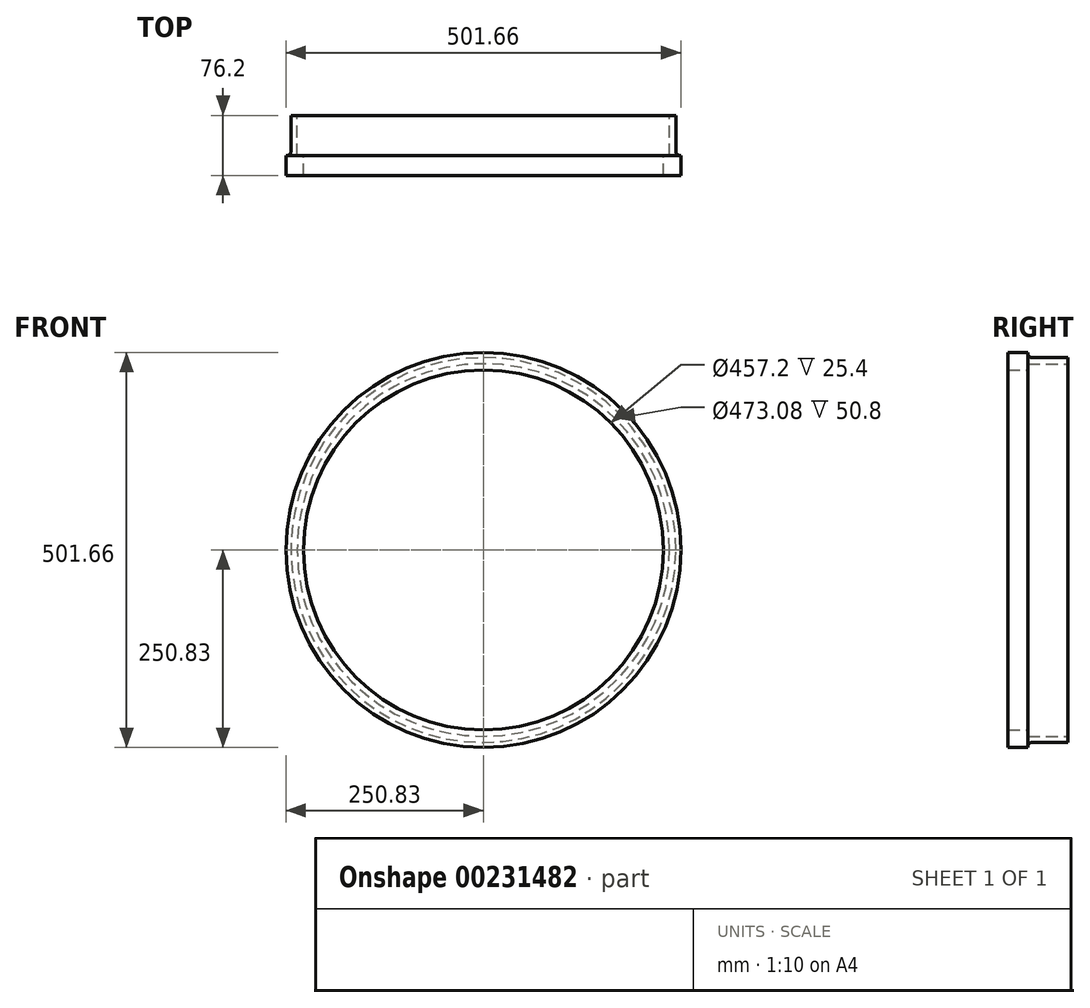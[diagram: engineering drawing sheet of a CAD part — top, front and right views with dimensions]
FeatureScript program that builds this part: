
annotation { "Feature Type Name" : "Feature", "Feature Type Description" : "" }
export const myFeature = defineFeature(function(context is Context, id is Id, definition is map)
    precondition{}
    {
        {
            var Q0;
            Q0=qCreatedBy(makeId("Front.planeOp"),FACE);
            var sketch = newSketch(context, id + "F0", { "sketchPlane" : qUnion([Q0])});
            skCircle(sketch, "E0", {"center": v(0, 0) * mm, "radius": 250.83 * mm});
            skCircle(sketch, "E1", {"center": v(0, 0) * mm, "radius": 228.6 * mm});
            skSolve(sketch);
        }
        {
            var Q0;
            Q0 = qSketchRegion(id + "F0", true);
            extrude(context, id + "F1", {"entities" : qUnion([Q0]), "depth" : 76.2 * mm});
        }
        {
            var Q0;
            Q0=makeQuery(id+"F1.opExtrude","CAP_FACE",FACE,{"disambiguationData":[OSD([sQuery(id+"F0.wireOp",EDGE,"E0"),sQuery(id+"F0.wireOp",EDGE,"E1")])],"isStart":true});
            var sketch = newSketch(context, id + "F2", { "sketchPlane" : qUnion([Q0])});
            skCircle(sketch, "E2", {"center": v(0, 0) * mm, "radius": 244.48 * mm});
            skCircle(sketch, "E3", {"center": v(0, 0) * mm, "radius": 250.83 * mm});
            skSolve(sketch);
        }
        {
            var Q0;
            Q0 = qSketchRegion(id + "F2", true);
            extrude(context, id + "F3", {"entities" : qUnion([Q0]), "operationType" : NewBodyOperationType.REMOVE, "oppositeDirection" : true, "depth" : 50.8 * mm});
        }
        {
            var Q0;
            Q0=makeQuery(id+"F3.boolean.opBoolean","COPY",EDGE,{"derivedFrom":makeQuery(id+"F3.opExtrude","CAP_EDGE",EDGE,{"disambiguationData":[OSD([sQuery(id+"F2.wireOp",EDGE,"E2")])],"isStart":false})});
            fillet(context, id + "F4", {"entities" : qUnion([Q0]), "radius" : 5.08 * mm, "tangentPropagation" : true, "allowEdgeOverflow" : false});
        }
        {
            var Q0;
            Q0=makeQuery(id+"F1.opExtrude","CAP_FACE",FACE,{"disambiguationData":[OSD([sQuery(id+"F0.wireOp",EDGE,"E0"),sQuery(id+"F0.wireOp",EDGE,"E1")])],"isStart":true});
            var sketch = newSketch(context, id + "F5", { "sketchPlane" : qUnion([Q0])});
            skCircle(sketch, "E4", {"center": v(0, 0) * mm, "radius": 236.54 * mm});
            skCircle(sketch, "E5", {"center": v(0, 0) * mm, "radius": 228.6 * mm});
            skSolve(sketch);
        }
        {
            var Q0;
            Q0 = qSketchRegion(id + "F5", true);
            extrude(context, id + "F6", {"entities" : qUnion([Q0]), "operationType" : NewBodyOperationType.REMOVE, "oppositeDirection" : true, "depth" : 50.8 * mm});
        }
    });
